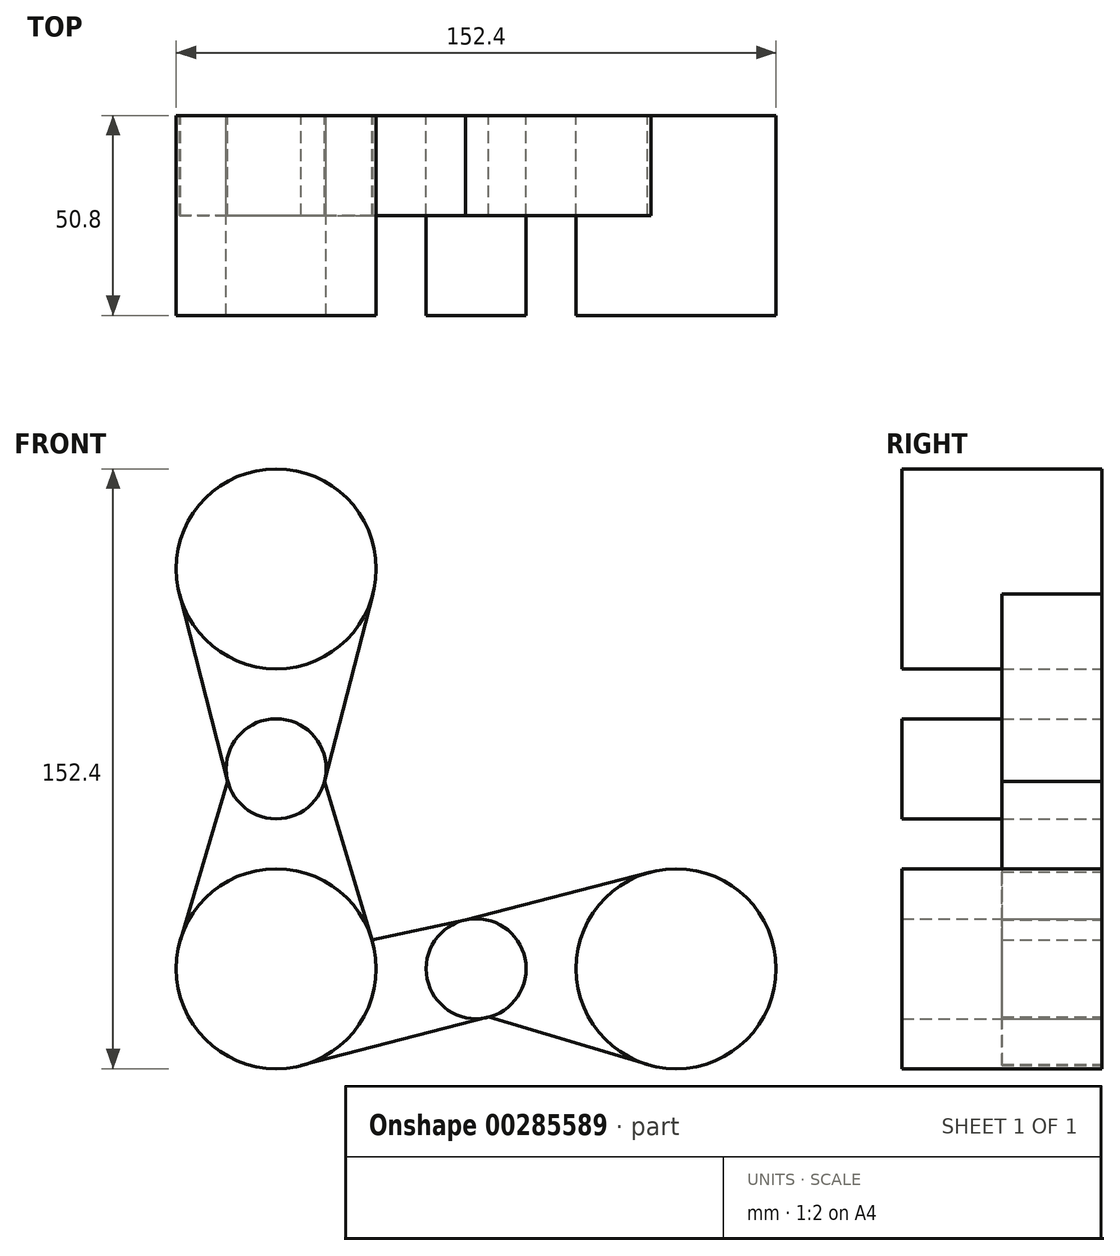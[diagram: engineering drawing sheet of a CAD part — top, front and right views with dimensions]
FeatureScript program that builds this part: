
annotation { "Feature Type Name" : "Feature", "Feature Type Description" : "" }
export const myFeature = defineFeature(function(context is Context, id is Id, definition is map)
    precondition{}
    {
        {
            var Q0;
            Q0=qCreatedBy(makeId("Front.planeOp"),FACE);
            var sketch = newSketch(context, id + "F0", { "sketchPlane" : qUnion([Q0])});
            skLineSegment(sketch, "E0", {"start": v(-146.8, -74.16) * mm, "end": v(-96, -74.16) * mm});
            skLineSegment(sketch, "E1", {"start": v(-96, -74.16) * mm, "end": v(-45.2, -74.16) * mm});
            skLineSegment(sketch, "E2", {"start": v(-146.8, -74.16) * mm, "end": v(-146.8, -23.36) * mm});
            skLineSegment(sketch, "E3", {"start": v(-146.8, -23.36) * mm, "end": v(-146.8, 27.44) * mm});
            skCircle(sketch, "E4", {"center": v(-146.8, 27.44) * mm, "radius": 25.4 * mm});
            skCircle(sketch, "E5", {"center": v(-45.2, -74.16) * mm, "radius": 25.4 * mm});
            skCircle(sketch, "E6", {"center": v(-146.8, -74.16) * mm, "radius": 25.4 * mm});
            skCircle(sketch, "E7", {"center": v(-146.8, -23.36) * mm, "radius": 12.7 * mm});
            skCircle(sketch, "E8", {"center": v(-96, -74.16) * mm, "radius": 12.7 * mm});
            skLineSegment(sketch, "E9", {"start": v(-171.4, 21.09) * mm, "end": v(-159.1, -26.54) * mm});
            skLineSegment(sketch, "E10", {"start": v(-159.1, -26.54) * mm, "end": v(-171.14, -66.9) * mm});
            skLineSegment(sketch, "E11", {"start": v(-122.2, 21.09) * mm, "end": v(-134.5, -26.54) * mm});
            skLineSegment(sketch, "E12", {"start": v(-134.5, -26.54) * mm, "end": v(-122.46, -66.9) * mm});
            skLineSegment(sketch, "E13", {"start": v(-122.46, -66.9) * mm, "end": v(-98.69, -61.75) * mm});
            skLineSegment(sketch, "E14", {"start": v(-98.69, -61.75) * mm, "end": v(-51.55, -49.57) * mm});
            skLineSegment(sketch, "E15", {"start": v(-140.45, -98.76) * mm, "end": v(-92.82, -86.46) * mm});
            skLineSegment(sketch, "E16", {"start": v(-92.82, -86.46) * mm, "end": v(-52.46, -98.5) * mm});
            skSolve(sketch);
        }
        {
            var Q0;
            {var subQ0=sQuery(id+"F0.wireOp",EDGE,"E4");var subQ1=makeQuery(id+"F0.imprint","INTERSECT",VERTEX,{"derivedFrom":[subQ0,sQuery(id+"F0.wireOp",EDGE,"E9")]});Q0=makeQuery(id+"F0.imprint","IMPRINT",FACE,{"disambiguationData":[TD([[makeQuery(id+"F0.imprint","IMPRINT",EDGE,{"disambiguationData":[TD([[subQ1,-1.0]])],"derivedFrom":subQ0}),1.0]])]});}
            var Q1;
            {var subQ0=sQuery(id+"F0.wireOp",EDGE,"E3");var subQ1=sQuery(id+"F0.wireOp",EDGE,"E2");var subQ2=makeQuery(id+"F0.imprint","INTERSECT",VERTEX,{"derivedFrom":[subQ1,subQ0]});Q1=makeQuery(id+"F0.imprint","IMPRINT",FACE,{"disambiguationData":[TD([[makeQuery(id+"F0.imprint","IMPRINT",EDGE,{"disambiguationData":[TD([[subQ2,1.0]])],"derivedFrom":subQ1}),1.0]])]});}
            var Q2;
            {var subQ0=sQuery(id+"F0.wireOp",EDGE,"E3");var subQ1=sQuery(id+"F0.wireOp",EDGE,"E2");var subQ2=makeQuery(id+"F0.imprint","INTERSECT",VERTEX,{"derivedFrom":[subQ1,subQ0]});Q2=makeQuery(id+"F0.imprint","IMPRINT",FACE,{"disambiguationData":[TD([[makeQuery(id+"F0.imprint","IMPRINT",EDGE,{"disambiguationData":[TD([[subQ2,1.0]])],"derivedFrom":subQ1}),-1.0]])]});}
            var Q3;
            {var subQ3=sQuery(id+"F0.wireOp",EDGE,"E2");var subQ5=sQuery(id+"F0.wireOp",EDGE,"E0");var subQ6=makeQuery(id+"F0.imprint","INTERSECT",VERTEX,{"derivedFrom":[subQ5,subQ3]});Q3=makeQuery(id+"F0.imprint","IMPRINT",FACE,{"disambiguationData":[TD([[makeQuery(id+"F0.imprint","IMPRINT",EDGE,{"disambiguationData":[TD([[subQ6,-1.0]])],"derivedFrom":subQ5}),-1.0]])]});}
            var Q4;
            {var subQ0=sQuery(id+"F0.wireOp",EDGE,"E2");var subQ1=sQuery(id+"F0.wireOp",EDGE,"E0");var subQ2=makeQuery(id+"F0.imprint","INTERSECT",VERTEX,{"derivedFrom":[subQ1,subQ0]});Q4=makeQuery(id+"F0.imprint","IMPRINT",FACE,{"disambiguationData":[TD([[makeQuery(id+"F0.imprint","IMPRINT",EDGE,{"disambiguationData":[TD([[subQ2,-1.0]])],"derivedFrom":subQ1}),1.0]])]});}
            var Q5;
            {var subQ0=sQuery(id+"F0.wireOp",EDGE,"E1");var subQ1=sQuery(id+"F0.wireOp",EDGE,"E0");var subQ2=makeQuery(id+"F0.imprint","INTERSECT",VERTEX,{"derivedFrom":[subQ1,subQ0]});Q5=makeQuery(id+"F0.imprint","IMPRINT",FACE,{"disambiguationData":[TD([[makeQuery(id+"F0.imprint","IMPRINT",EDGE,{"disambiguationData":[TD([[subQ2,1.0]])],"derivedFrom":subQ1}),1.0]])]});}
            var Q6;
            {var subQ0=sQuery(id+"F0.wireOp",EDGE,"E5");var subQ1=makeQuery(id+"F0.imprint","INTERSECT",VERTEX,{"derivedFrom":[subQ0,sQuery(id+"F0.wireOp",EDGE,"E14")]});Q6=makeQuery(id+"F0.imprint","IMPRINT",FACE,{"disambiguationData":[TD([[makeQuery(id+"F0.imprint","IMPRINT",EDGE,{"disambiguationData":[TD([[subQ1,-1.0]])],"derivedFrom":subQ0}),1.0]])]});}
            var Q7;
            {var subQ0=sQuery(id+"F0.wireOp",EDGE,"E1");var subQ1=sQuery(id+"F0.wireOp",EDGE,"E0");var subQ2=makeQuery(id+"F0.imprint","INTERSECT",VERTEX,{"derivedFrom":[subQ1,subQ0]});Q7=makeQuery(id+"F0.imprint","IMPRINT",FACE,{"disambiguationData":[TD([[makeQuery(id+"F0.imprint","IMPRINT",EDGE,{"disambiguationData":[TD([[subQ2,1.0]])],"derivedFrom":subQ1}),-1.0]])]});}
            extrude(context, id + "F1", {"entities" : qUnion([Q0, Q1, Q2, Q3, Q4, Q5, Q6, Q7]), "depth" : 50.8 * mm});
        }
        {
            var Q0;
            {var subQ5=sQuery(id+"F0.wireOp",EDGE,"E11");Q0=makeQuery(id+"F0.imprint","IMPRINT",FACE,{"disambiguationData":[TD([[makeQuery(id+"F0.imprint","IMPRINT",EDGE,{"derivedFrom":subQ5}),-1.0]])]});}
            var Q1;
            {var subQ5=sQuery(id+"F0.wireOp",EDGE,"E9");Q1=makeQuery(id+"F0.imprint","IMPRINT",FACE,{"disambiguationData":[TD([[makeQuery(id+"F0.imprint","IMPRINT",EDGE,{"derivedFrom":subQ5}),1.0]])]});}
            var Q2;
            {var subQ5=sQuery(id+"F0.wireOp",EDGE,"E10");Q2=makeQuery(id+"F0.imprint","IMPRINT",FACE,{"disambiguationData":[TD([[makeQuery(id+"F0.imprint","IMPRINT",EDGE,{"derivedFrom":subQ5}),1.0]])]});}
            var Q3;
            {var subQ5=sQuery(id+"F0.wireOp",EDGE,"E12");Q3=makeQuery(id+"F0.imprint","IMPRINT",FACE,{"disambiguationData":[TD([[makeQuery(id+"F0.imprint","IMPRINT",EDGE,{"derivedFrom":subQ5}),-1.0]])]});}
            var Q4;
            {var subQ5=sQuery(id+"F0.wireOp",EDGE,"E14");Q4=makeQuery(id+"F0.imprint","IMPRINT",FACE,{"disambiguationData":[TD([[makeQuery(id+"F0.imprint","IMPRINT",EDGE,{"derivedFrom":subQ5}),-1.0]])]});}
            var Q5;
            {var subQ5=sQuery(id+"F0.wireOp",EDGE,"E16");Q5=makeQuery(id+"F0.imprint","IMPRINT",FACE,{"disambiguationData":[TD([[makeQuery(id+"F0.imprint","IMPRINT",EDGE,{"derivedFrom":subQ5}),1.0]])]});}
            var Q6;
            {var subQ5=sQuery(id+"F0.wireOp",EDGE,"E15");Q6=makeQuery(id+"F0.imprint","IMPRINT",FACE,{"disambiguationData":[TD([[makeQuery(id+"F0.imprint","IMPRINT",EDGE,{"derivedFrom":subQ5}),1.0]])]});}
            var Q7;
            {var subQ5=sQuery(id+"F0.wireOp",EDGE,"E13");Q7=makeQuery(id+"F0.imprint","IMPRINT",FACE,{"disambiguationData":[TD([[makeQuery(id+"F0.imprint","IMPRINT",EDGE,{"derivedFrom":subQ5}),-1.0]])]});}
            extrude(context, id + "F2", {"entities" : qUnion([Q0, Q1, Q2, Q3, Q4, Q5, Q6, Q7]), "depth" : 25.4 * mm});
        }
    });
